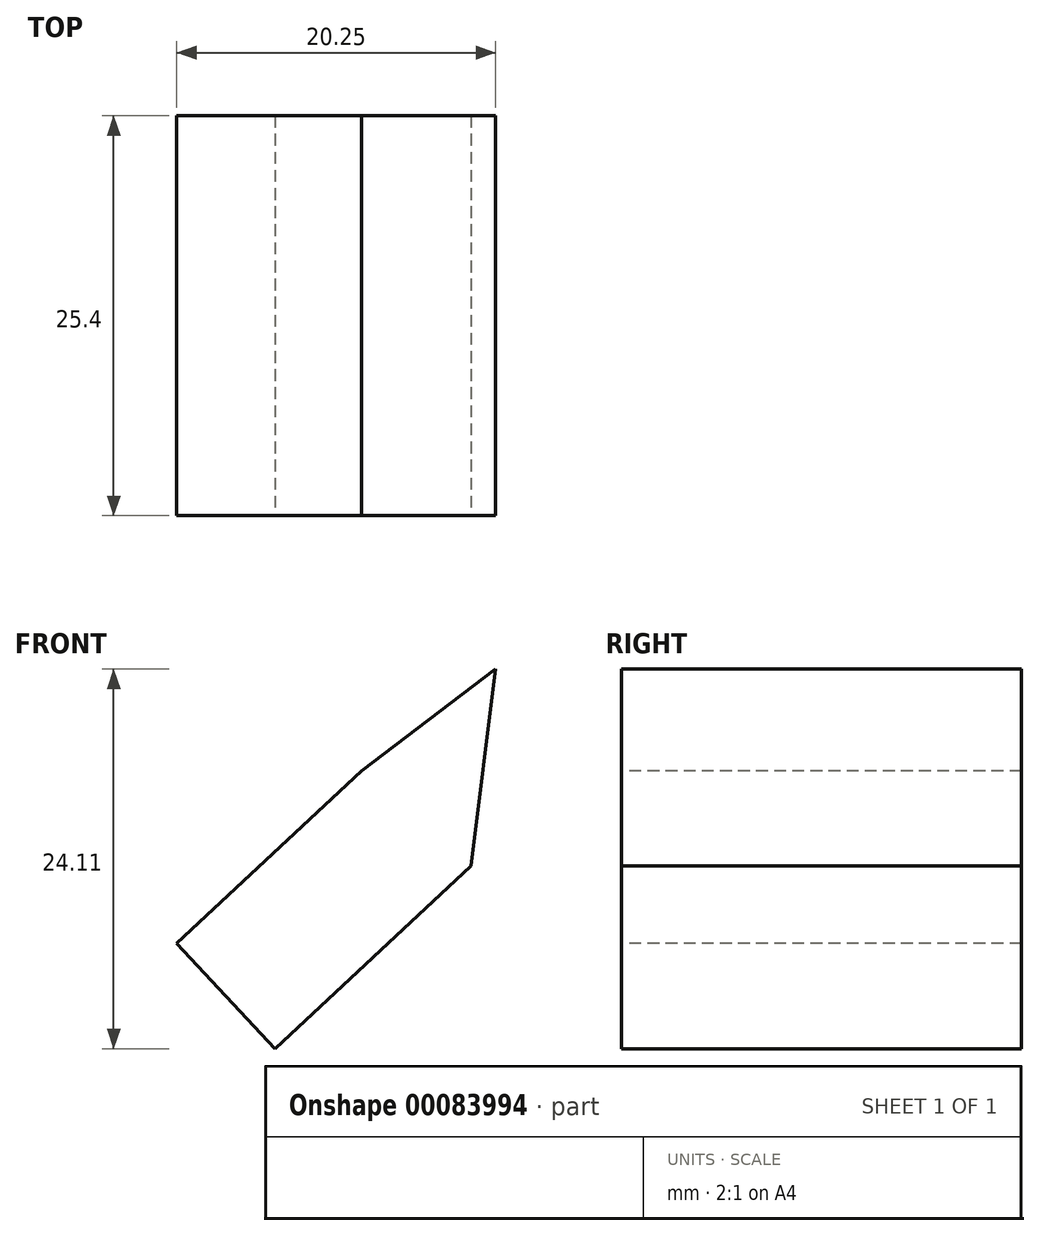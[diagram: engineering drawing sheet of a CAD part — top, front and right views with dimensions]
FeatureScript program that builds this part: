
annotation { "Feature Type Name" : "Feature", "Feature Type Description" : "" }
export const myFeature = defineFeature(function(context is Context, id is Id, definition is map)
    precondition{}
    {
        {
            var Q0;
            Q0=qCreatedBy(makeId("Front.planeOp"),FACE);
            var sketch = newSketch(context, id + "F0", { "sketchPlane" : qUnion([Q0])});
            skLineSegment(sketch, "E0", {"start": v(-27.35, 53.27) * mm, "end": v(-35.85, 46.8) * mm});
            skLineSegment(sketch, "E1", {"start": v(-35.85, 46.8) * mm, "end": v(-47.6, 35.85) * mm});
            skLineSegment(sketch, "E2", {"start": v(-47.6, 35.85) * mm, "end": v(-41.37, 29.16) * mm});
            skLineSegment(sketch, "E3", {"start": v(-41.37, 29.16) * mm, "end": v(-28.92, 40.76) * mm});
            skLineSegment(sketch, "E4", {"start": v(-28.92, 40.76) * mm, "end": v(-27.35, 53.27) * mm});
            skSolve(sketch);
        }
        {
            var Q0;
            Q0=makeQuery(id+"F0.imprint","IMPRINT",FACE,{"disambiguationData":[TD([[makeQuery(id+"F0.imprint","IMPRINT",EDGE,{"derivedFrom":sQuery(id+"F0.wireOp",EDGE,"E0")}),1.0]])]});
            extrude(context, id + "F1", {"entities" : qUnion([Q0]), "oppositeDirection" : true, "depth" : 25.4 * mm});
        }
    });
